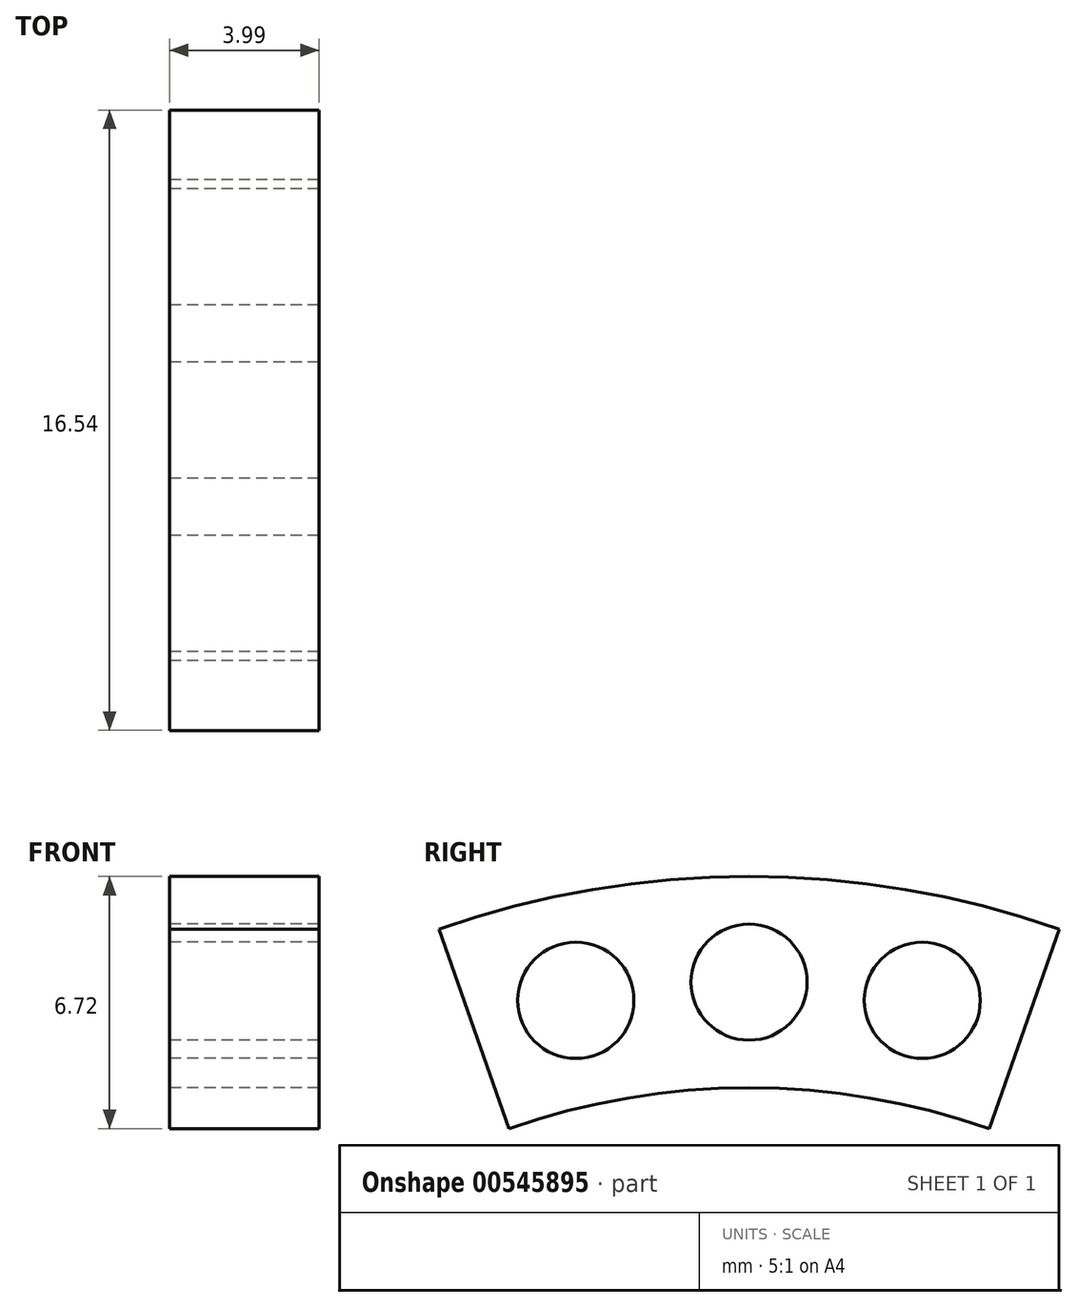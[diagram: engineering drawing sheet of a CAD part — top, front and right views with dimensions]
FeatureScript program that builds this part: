
annotation { "Feature Type Name" : "Feature", "Feature Type Description" : "" }
export const myFeature = defineFeature(function(context is Context, id is Id, definition is map)
    precondition{}
    {
        {
            var Q0;
            Q0=qCreatedBy(makeId("Right.planeOp"),FACE);
            var sketch = newSketch(context, id + "F0", { "sketchPlane" : qUnion([Q0])});
            skCircle(sketch, "E0", {"center": v(0, 0) * mm, "radius": 23.42 * mm, "construction": true});
            skLineSegment(sketch, "E1", {"start": v(0, 0) * mm, "end": v(-4.87, 22.9) * mm, "construction": true});
            skLineSegment(sketch, "E2", {"start": v(0, 0) * mm, "end": v(4.87, 22.9) * mm, "construction": true});
            skCircle(sketch, "E3", {"center": v(0, 0) * mm, "radius": 21.03 * mm, "construction": true});
            skCircle(sketch, "E4", {"center": v(0, 0) * mm, "radius": 22.23 * mm, "construction": true});
            skCircle(sketch, "E5", {"center": v(4.62, 21.74) * mm, "radius": 1.2 * mm, "construction": true});
            skCircle(sketch, "E6", {"center": v(-4.62, 21.74) * mm, "radius": 1.2 * mm, "construction": true});
            skCircle(sketch, "E7", {"center": v(0, 22.23) * mm, "radius": 1.2 * mm, "construction": true});
            skCircle(sketch, "E8", {"center": v(4.62, 21.74) * mm, "radius": 1.98 * mm, "construction": true});
            skCircle(sketch, "E9", {"center": v(0, 22.23) * mm, "radius": 1.98 * mm, "construction": true});
            skCircle(sketch, "E10", {"center": v(-4.62, 21.74) * mm, "radius": 1.98 * mm, "construction": true});
            skSolve(sketch);
        }
        {
            var Q0;
            Q0=qCreatedBy(makeId("Right.planeOp"),FACE);
            var sketch = newSketch(context, id + "F1", { "sketchPlane" : qUnion([Q0])});
            skCircle(sketch, "E11", {"center": v(4.62, 21.74) * mm, "radius": 1.55 * mm});
            skCircle(sketch, "E12", {"center": v(0, 22.23) * mm, "radius": 1.55 * mm});
            skCircle(sketch, "E13", {"center": v(-4.62, 21.74) * mm, "radius": 1.55 * mm});
            skLineSegment(sketch, "E14", {"start": v(0, 0) * mm, "end": v(-7.73, 22.1) * mm, "construction": true});
            skLineSegment(sketch, "E15", {"start": v(0, 0) * mm, "end": v(7.73, 22.1) * mm, "construction": true});
            skArc(sketch, "E16", {"start": v(-8.27, 23.64) * mm, "mid": v(0, 25.04) * mm, "end": v(8.27, 23.64) * mm});
            skArc(sketch, "E17", {"start": v(-6.4, 18.32) * mm, "mid": v(0, 19.4) * mm, "end": v(6.4, 18.32) * mm});
            skLineSegment(sketch, "E18", {"start": v(-8.27, 23.64) * mm, "end": v(-6.4, 18.32) * mm});
            skLineSegment(sketch, "E19", {"start": v(8.27, 23.64) * mm, "end": v(6.4, 18.32) * mm});
            skSolve(sketch);
        }
        {
            var Q0;
            Q0 = qSketchRegion(id + "F1", true);
            extrude(context, id + "F2", {"entities" : qUnion([Q0]), "depth" : 4 * mm, "offsetDistance" : 25.4 * mm});
        }
    });
